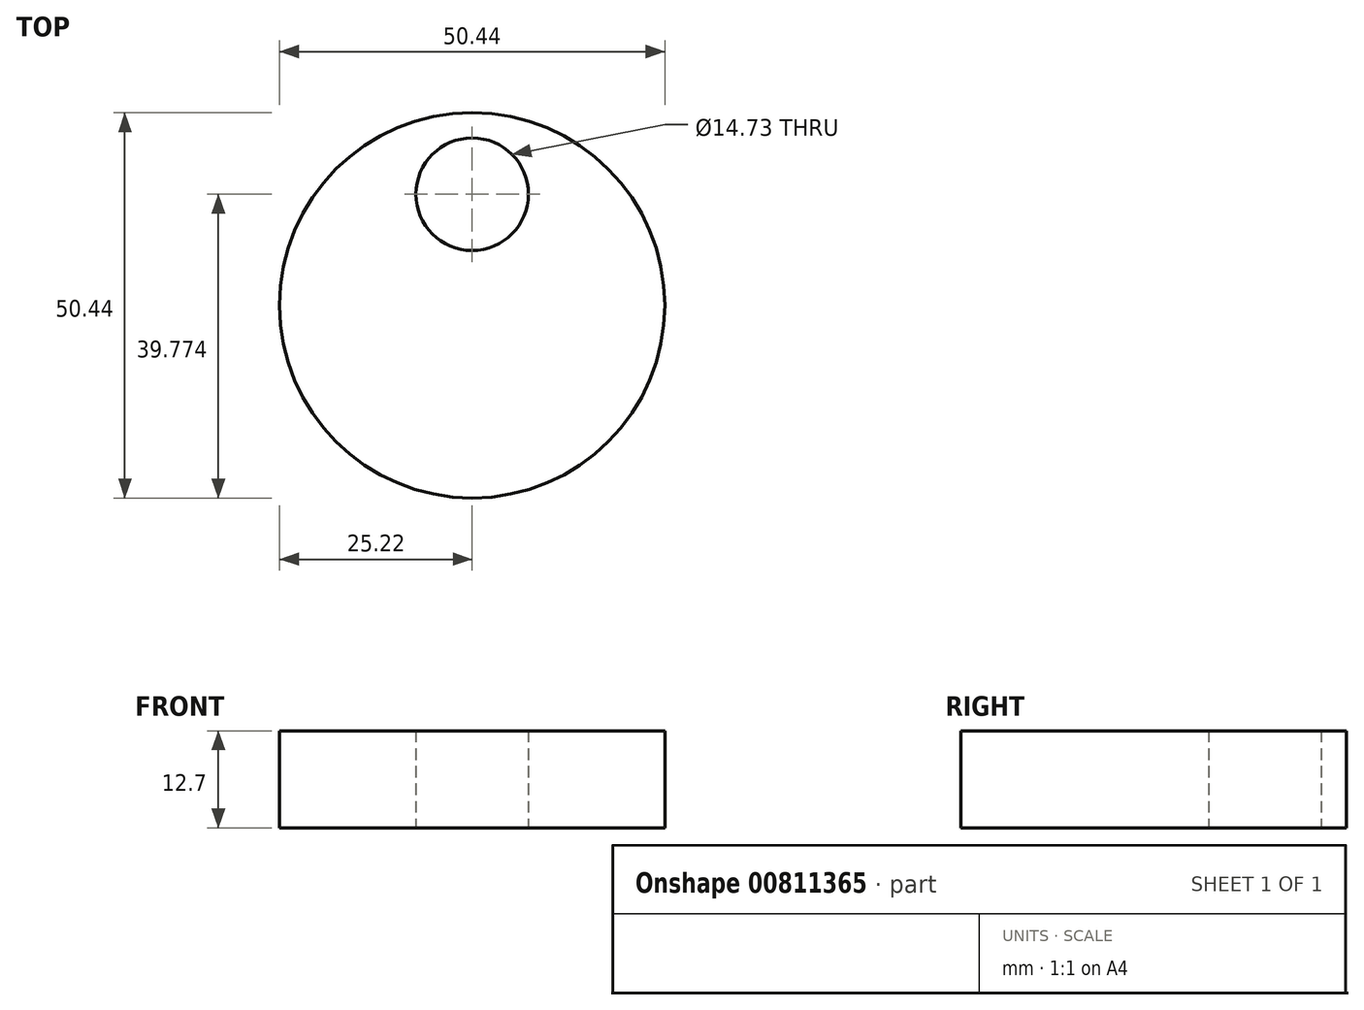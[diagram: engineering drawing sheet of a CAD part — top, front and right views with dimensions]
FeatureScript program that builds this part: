
annotation { "Feature Type Name" : "Feature", "Feature Type Description" : "" }
export const myFeature = defineFeature(function(context is Context, id is Id, definition is map)
    precondition{}
    {
        {
            var Q0;
            Q0=qCreatedBy(makeId("Top.planeOp"),FACE);
            var sketch = newSketch(context, id + "F0", { "sketchPlane" : qUnion([Q0])});
            skCircle(sketch, "E0", {"center": v(0, 0) * mm, "radius": 25.22 * mm});
            skCircle(sketch, "E1", {"center": v(0, 14.55) * mm, "radius": 7.37 * mm});
            skSolve(sketch);
        }
        {
            var Q0;
            Q0=makeQuery(id+"F0.imprint","IMPRINT",FACE,{"disambiguationData":[TD([[makeQuery(id+"F0.imprint","IMPRINT",EDGE,{"derivedFrom":sQuery(id+"F0.wireOp",EDGE,"E0")}),1.0]])]});
            extrude(context, id + "F1", {"entities" : qUnion([Q0]), "depth" : 12.7 * mm, "offsetDistance" : 25.4 * mm});
        }
    });
